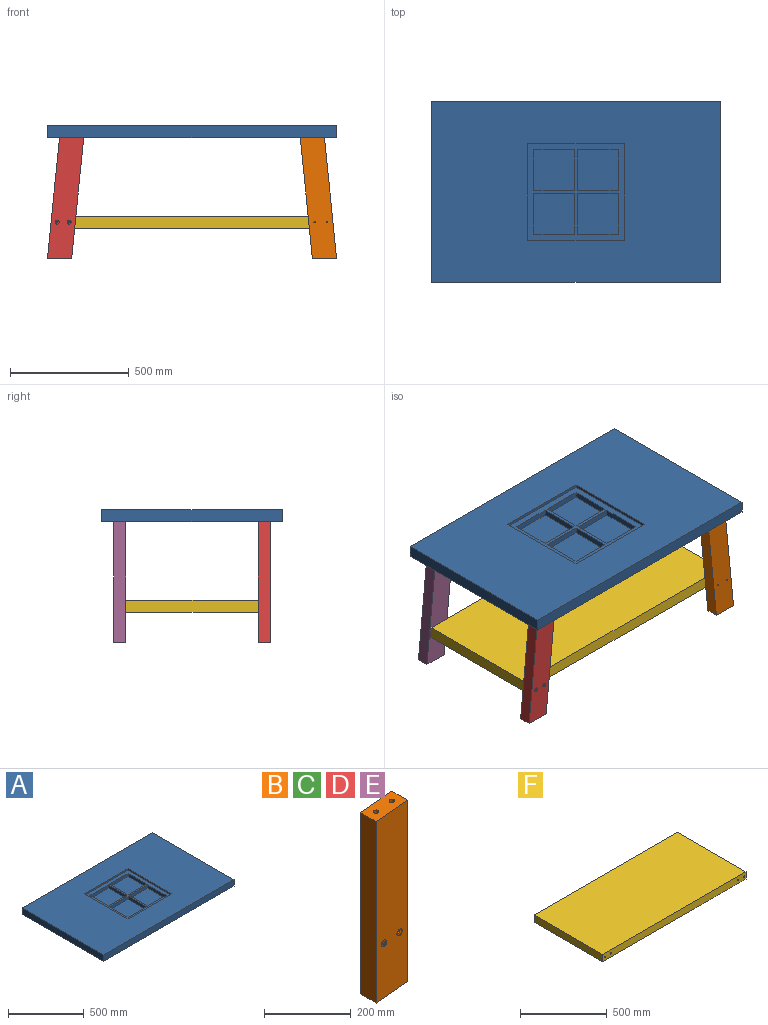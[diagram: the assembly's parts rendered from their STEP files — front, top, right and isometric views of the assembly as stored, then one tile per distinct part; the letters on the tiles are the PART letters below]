
ASSEMBLY  parts=6 mates=15
PART A: 47 faces, bbox 1219.2x762x50.8 mm
  f0: plane 1219.2x762mm, normal (0,0,1), area 763869.4mm2, adj f1,f2,f3,f4,f23,f24,f25,f26
  f1: plane 1219.2x50.8mm, normal (0,1,0), area 61935.4mm2, adj f0,f2,f4,f5
  f2: plane 762x50.8mm, normal (-1,0,0), area 38709.6mm2, adj f0,f1,f3,f5
  f3: plane 1219.2x50.8mm, normal (0,-1,0), area 61935.4mm2, adj f0,f2,f4,f5
  f4: plane 762x50.8mm, normal (1,0,0), area 38709.6mm2, adj f0,f1,f3,f5
  f5: plane 1219.2x762mm, normal (0,0,-1), area 928017mm2, adj f1,f2,f3,f4,f6,f8,f10,f12
  f6: cylinder r=6.35mm len=12.7mm, axis (0,0,-1), area 506.7mm2, adj f5,f7
  f7: plane 12.7x12.7mm, normal (0,0,-1), area 126.7mm2, adj f6
  f8: cylinder r=6.35mm len=12.7mm, axis (0,0,-1), area 506.7mm2, adj f5,f9
  f9: plane 12.7x12.7mm, normal (0,0,-1), area 126.7mm2, adj f8
  f10: cylinder r=6.35mm len=12.7mm, axis (0,0,-1), area 506.7mm2, adj f5,f11
  f11: plane 12.7x12.7mm, normal (0,0,-1), area 126.7mm2, adj f10
  f12: cylinder r=6.35mm len=12.7mm, axis (0,0,-1), area 506.7mm2, adj f5,f13
  f13: plane 12.7x12.7mm, normal (0,0,-1), area 126.7mm2, adj f12
  f14: cylinder r=6.35mm len=12.7mm, axis (0,0,-1), area 506.7mm2, adj f5,f15
  f15: plane 12.7x12.7mm, normal (0,0,-1), area 126.7mm2, adj f14
  f16: cylinder r=6.35mm len=12.7mm, axis (0,0,-1), area 506.7mm2, adj f5,f17
  f17: plane 12.7x12.7mm, normal (0,0,-1), area 126.7mm2, adj f16
  f18: cylinder r=6.35mm len=12.7mm, axis (0,0,-1), area 506.7mm2, adj f5,f19
  f19: plane 12.7x12.7mm, normal (0,0,-1), area 126.7mm2, adj f18
  f20: cylinder r=6.35mm len=12.7mm, axis (0,0,-1), area 506.7mm2, adj f5,f21
  f21: plane 12.7x12.7mm, normal (0,0,-1), area 126.7mm2, adj f20
  f22: plane 406.4x406.4mm, normal (0,0,1), area 47580.6mm2, adj f23,f24,f25,f26,f28,f29,f30,f31
  f23: plane 406.4x12.7mm, normal (0,1,0), area 5161.3mm2, adj f0,f22,f24,f26
  f24: plane 406.4x12.7mm, normal (-1,0,0), area 5161.3mm2, adj f0,f22,f23,f25
  f25: plane 406.4x12.7mm, normal (0,-1,0), area 5161.3mm2, adj f0,f22,f24,f26
  f26: plane 406.4x12.7mm, normal (1,0,0), area 5161.3mm2, adj f0,f22,f23,f25
  f27: plane 171.45x171.45mm, normal (0,0,1), area 29395.1mm2, adj f28,f29,f30,f31
  f28: plane 171.45x25.4mm, normal (0,1,0), area 4354.8mm2, adj f22,f27,f29,f31
  f29: plane 171.45x25.4mm, normal (1,0,0), area 4354.8mm2, adj f22,f27,f28,f30
  f30: plane 171.45x25.4mm, normal (0,-1,0), area 4354.8mm2, adj f22,f27,f29,f31
  f31: plane 171.45x25.4mm, normal (-1,0,0), area 4354.8mm2, adj f22,f27,f28,f30
  f32: plane 171.45x171.45mm, normal (0,0,1), area 29395.1mm2, adj f33,f34,f35,f36
  f33: plane 171.45x25.4mm, normal (1,0,0), area 4354.8mm2, adj f22,f32,f34,f36
  f34: plane 171.45x25.4mm, normal (0,-1,0), area 4354.8mm2, adj f22,f32,f33,f35
  f35: plane 171.45x25.4mm, normal (-1,0,0), area 4354.8mm2, adj f22,f32,f34,f36
  f36: plane 171.45x25.4mm, normal (0,1,0), area 4354.8mm2, adj f22,f32,f33,f35
  f37: plane 171.45x171.45mm, normal (0,0,1), area 29395.1mm2, adj f38,f39,f40,f41
  f38: plane 171.45x25.4mm, normal (0,-1,0), area 4354.8mm2, adj f22,f37,f39,f41
  f39: plane 171.45x25.4mm, normal (-1,0,0), area 4354.8mm2, adj f22,f37,f38,f40
  f40: plane 171.45x25.4mm, normal (0,1,0), area 4354.8mm2, adj f22,f37,f39,f41
  f41: plane 171.45x25.4mm, normal (1,0,0), area 4354.8mm2, adj f22,f37,f38,f40
  f42: plane 171.45x171.45mm, normal (0,0,1), area 29395.1mm2, adj f43,f44,f45,f46
  f43: plane 171.45x25.4mm, normal (-1,0,0), area 4354.8mm2, adj f22,f42,f44,f46
  f44: plane 171.45x25.4mm, normal (0,1,0), area 4354.8mm2, adj f22,f42,f43,f45
  f45: plane 171.45x25.4mm, normal (1,0,0), area 4354.8mm2, adj f22,f42,f44,f46
  f46: plane 171.45x25.4mm, normal (0,-1,0), area 4354.8mm2, adj f22,f42,f43,f45
PART B: 16 faces, bbox 101.6x50.8x520.7 mm
  f0: cylinder r=3.37mm len=48.42mm, axis (0,-1,0), area 1026.3mm2, adj f7,f14
  f1: cylinder r=3.37mm len=48.42mm, axis (0,-1,0), area 1026.3mm2, adj f7,f12
  f2: plane 101.6x50.8mm, normal (-0.1,0,1), area 4933.7mm2, adj f3,f5,f6,f7,f8,f10
  f3: plane 510.53x50.8mm, normal (-1,0,0), area 25935.1mm2, adj f2,f4,f6,f7
  f4: plane 101.6x50.8mm, normal (0.1,0,-1), area 5187mm2, adj f3,f5,f6,f7
  f5: plane 510.53x50.8mm, normal (1,0,0), area 25935.1mm2, adj f2,f4,f6,f7
  f6: plane 520.69x101.6mm, normal (0,-1,0), area 51391.2mm2, adj f2,f3,f4,f5,f13,f15
  f7: plane 520.69x101.6mm, normal (0,1,0), area 51798.7mm2, adj f0,f1,f2,f3,f4,f5
  f8: cylinder r=6.35mm len=13.9mm, axis (-0.1,0,1), area 506.7mm2, adj f2,f9
  f9: plane 12.7x12.64mm, normal (-0.1,0,1), area 126.7mm2, adj f8
  f10: cylinder r=6.35mm len=13.9mm, axis (-0.1,0,1), area 506.7mm2, adj f2,f11
  f11: plane 12.7x12.64mm, normal (-0.1,0,1), area 126.7mm2, adj f10
  f12: plane 17.46x17.46mm, normal (0,-1,0), area 203.7mm2, adj f1,f13
  f13: cylinder r=8.73mm len=17.46mm, axis (0,-1,0), area 130.6mm2, adj f6,f12
  f14: plane 17.46x17.46mm, normal (0,-1,0), area 203.7mm2, adj f0,f15
  f15: cylinder r=8.73mm len=17.46mm, axis (0,-1,0), area 130.6mm2, adj f6,f14
PART C: same geometry as B
PART D: same geometry as B
PART E: same geometry as B
PART F: 22 faces, bbox 1168.4x558.8x50.8 mm
  f0: plane 558.8x50.8mm, normal (1,0,0), area 28387mm2, adj f1,f3,f4,f5
  f1: plane 1168.4x50.8mm, normal (0,1,0), area 59069.7mm2, adj f0,f2,f4,f5,f14,f16,f18,f20
  f2: plane 558.8x50.8mm, normal (-1,0,0), area 28387mm2, adj f1,f3,f4,f5
  f3: plane 1168.4x50.8mm, normal (0,-1,0), area 59069.7mm2, adj f0,f2,f4,f5,f6,f8,f10,f12
  f4: plane 1168.4x558.8mm, normal (0,0,1), area 652901.9mm2, adj f0,f1,f2,f3
  f5: plane 1168.4x558.8mm, normal (0,0,-1), area 652901.9mm2, adj f0,f1,f2,f3
  f6: cylinder r=4.76mm len=25.4mm, axis (0,-1,0), area 760.1mm2, adj f3,f7
  f7: plane 9.53x9.53mm, normal (0,-1,0), area 71.3mm2, adj f6
  f8: cylinder r=4.76mm len=25.4mm, axis (0,-1,0), area 760.1mm2, adj f3,f9
  f9: plane 9.53x9.53mm, normal (0,-1,0), area 71.3mm2, adj f8
  f10: cylinder r=4.76mm len=25.4mm, axis (0,-1,0), area 760.1mm2, adj f3,f11
  f11: plane 9.53x9.53mm, normal (0,-1,0), area 71.3mm2, adj f10
  f12: cylinder r=4.76mm len=25.4mm, axis (0,-1,0), area 760.1mm2, adj f3,f13
  f13: plane 9.53x9.53mm, normal (0,-1,0), area 71.3mm2, adj f12
  f14: cylinder r=4.76mm len=25.4mm, axis (0,1,0), area 760.1mm2, adj f1,f15
  f15: plane 9.53x9.53mm, normal (0,1,0), area 71.3mm2, adj f14
  f16: cylinder r=4.76mm len=25.4mm, axis (0,1,0), area 760.1mm2, adj f1,f17
  f17: plane 9.53x9.53mm, normal (0,1,0), area 71.3mm2, adj f16
  f18: cylinder r=4.76mm len=25.4mm, axis (0,1,0), area 760.1mm2, adj f1,f19
  f19: plane 9.53x9.53mm, normal (0,1,0), area 71.3mm2, adj f18
  f20: cylinder r=4.76mm len=25.4mm, axis (0,1,0), area 760.1mm2, adj f1,f21
  f21: plane 9.53x9.53mm, normal (0,1,0), area 71.3mm2, adj f20
PLACE A at identity
PLACE B rot(axis=(0.05,0,-1),180deg) t=(533.4,-330.2,-254)mm
PLACE C rot(axis=(-0.05,0,1),180deg) t=(533.4,279.4,-254)mm
PLACE D rot(axis=(0,1,0),5.7deg) t=(-533.4,-279.4,-254)mm
PLACE E rot(axis=(0,1,0),5.7deg) t=(-533.4,330.2,-254)mm
PLACE F t=(-1.69,0,-381)mm
MATE planar D.f10 <-> A.f6  axis (0,0,1) through (-533.4,-304.8,0)mm
MATE cylindrical F.f12 <-> D.f1  axis (0,-1,0) through (-568.96,-279.4,-355.6)mm
MATE cylindrical E.f10 <-> A.f16  axis (0,0,1) through (-533.4,304.8,0)mm
MATE parallel B.f7 <-> A.f3  axis (0,-1,0) through (533.31,-330.2,-253.05)mm
MATE cylindrical D.f10 <-> A.f6  axis (0,0,1) through (-533.4,-304.8,0)mm
MATE parallel D.f6 <-> A.f3  axis (0,-1,0) through (-533.31,-330.2,-253.05)mm
MATE parallel F.f4 <-> A.f5  axis (0,0,1) through (-1.69,0,-330.2)mm
MATE planar A.f20 <-> B.f10  axis (0,0,-1) through (533.4,-304.8,0)mm
MATE planar E.f10 <-> A.f16  axis (0,0,1) through (-533.4,304.8,0)mm
MATE cylindrical C.f10 <-> A.f18  axis (0,0,1) through (533.4,304.8,0)mm
MATE planar A.f18 <-> C.f10  axis (0,0,-1) through (533.4,304.8,0)mm
MATE cylindrical B.f10 <-> A.f20  axis (0,0,1) through (533.4,-304.8,0)mm
MATE parallel C.f6 <-> A.f1  axis (0,1,0) through (533.31,330.2,-253.05)mm
MATE parallel E.f7 <-> A.f1  axis (0,1,0) through (-533.31,330.2,-253.05)mm
MATE planar F.f12 <-> D.f1  axis (0,-1,0) through (-568.96,-279.4,-355.6)mm
